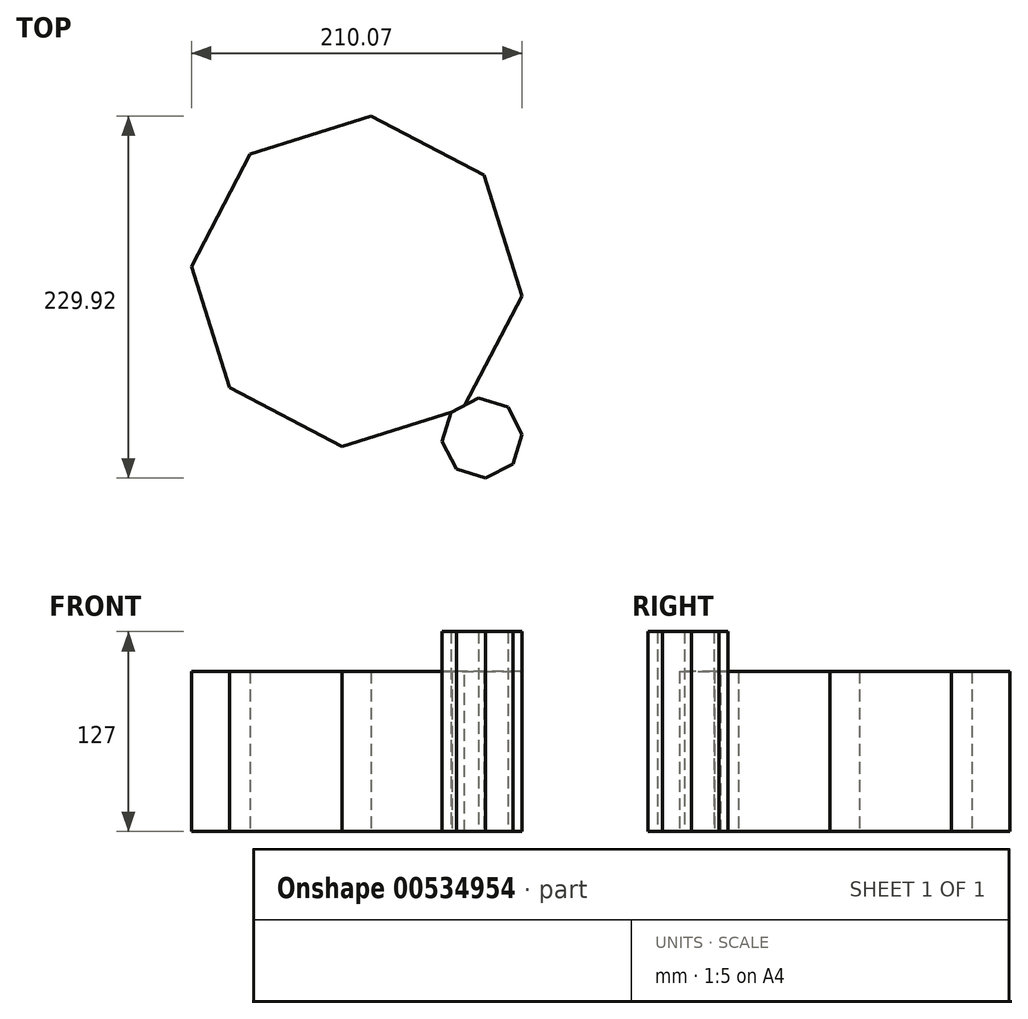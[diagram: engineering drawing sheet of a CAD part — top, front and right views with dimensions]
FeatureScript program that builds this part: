
annotation { "Feature Type Name" : "Feature", "Feature Type Description" : "" }
export const myFeature = defineFeature(function(context is Context, id is Id, definition is map)
    precondition{}
    {
        {
            var Q0;
            Q0=qCreatedBy(makeId("Top.planeOp"),FACE);
            var sketch = newSketch(context, id + "F0", { "sketchPlane" : qUnion([Q0])});
            skCircle(sketch, "E0.cCircle", {"center": v(8.27, -10.03) * mm, "radius": 105.34 * mm, "construction": true});
            skLineSegment(sketch, "E0.0", {"start": v(75.86, -90.82) * mm, "end": v(-1.07, -114.95) * mm});
            skLineSegment(sketch, "E0.1", {"start": v(-1.07, -114.95) * mm, "end": v(-72.53, -77.62) * mm});
            skLineSegment(sketch, "E0.2", {"start": v(-72.53, -77.62) * mm, "end": v(-96.66, -0.7) * mm});
            skLineSegment(sketch, "E0.3", {"start": v(-96.66, -0.7) * mm, "end": v(-59.32, 70.77) * mm});
            skLineSegment(sketch, "E0.4", {"start": v(-59.32, 70.77) * mm, "end": v(17.6, 94.9) * mm});
            skLineSegment(sketch, "E0.5", {"start": v(17.6, 94.9) * mm, "end": v(89.06, 57.56) * mm});
            skLineSegment(sketch, "E0.6", {"start": v(89.06, 57.56) * mm, "end": v(113.19, -19.36) * mm});
            skLineSegment(sketch, "E0.7", {"start": v(113.19, -19.36) * mm, "end": v(75.86, -90.82) * mm});
            skSolve(sketch);
        }
        {
            var Q0;
            Q0 = qSketchRegion(id + "F0", true);
            extrude(context, id + "F1", {"entities" : qUnion([Q0]), "depth" : 101.6 * mm, "offsetDistance" : 25.4 * mm});
        }
        {
            var Q0;
            Q0=qCreatedBy(makeId("Top.planeOp"),FACE);
            var sketch = newSketch(context, id + "F2", { "sketchPlane" : qUnion([Q0])});
            skCircle(sketch, "E1.cCircle", {"center": v(88, -109.62) * mm, "radius": 25.51 * mm, "construction": true});
            skLineSegment(sketch, "E1.0", {"start": v(90.3, -135.02) * mm, "end": v(71.66, -129.2) * mm});
            skLineSegment(sketch, "E1.1", {"start": v(71.66, -129.2) * mm, "end": v(62.6, -111.92) * mm});
            skLineSegment(sketch, "E1.2", {"start": v(62.6, -111.92) * mm, "end": v(68.4, -93.28) * mm});
            skLineSegment(sketch, "E1.3", {"start": v(68.4, -93.28) * mm, "end": v(85.7, -84.2) * mm});
            skLineSegment(sketch, "E1.4", {"start": v(85.7, -84.2) * mm, "end": v(104.34, -90.02) * mm});
            skLineSegment(sketch, "E1.5", {"start": v(104.34, -90.02) * mm, "end": v(113.4, -107.32) * mm});
            skLineSegment(sketch, "E1.6", {"start": v(113.4, -107.32) * mm, "end": v(107.6, -125.96) * mm});
            skLineSegment(sketch, "E1.7", {"start": v(107.6, -125.96) * mm, "end": v(90.3, -135.02) * mm});
            skSolve(sketch);
        }
        {
            var Q0;
            Q0 = qSketchRegion(id + "F2", true);
            extrude(context, id + "F3", {"entities" : qUnion([Q0]), "operationType" : NewBodyOperationType.ADD, "depth" : 127 * mm, "offsetDistance" : 25.4 * mm});
        }
    });
